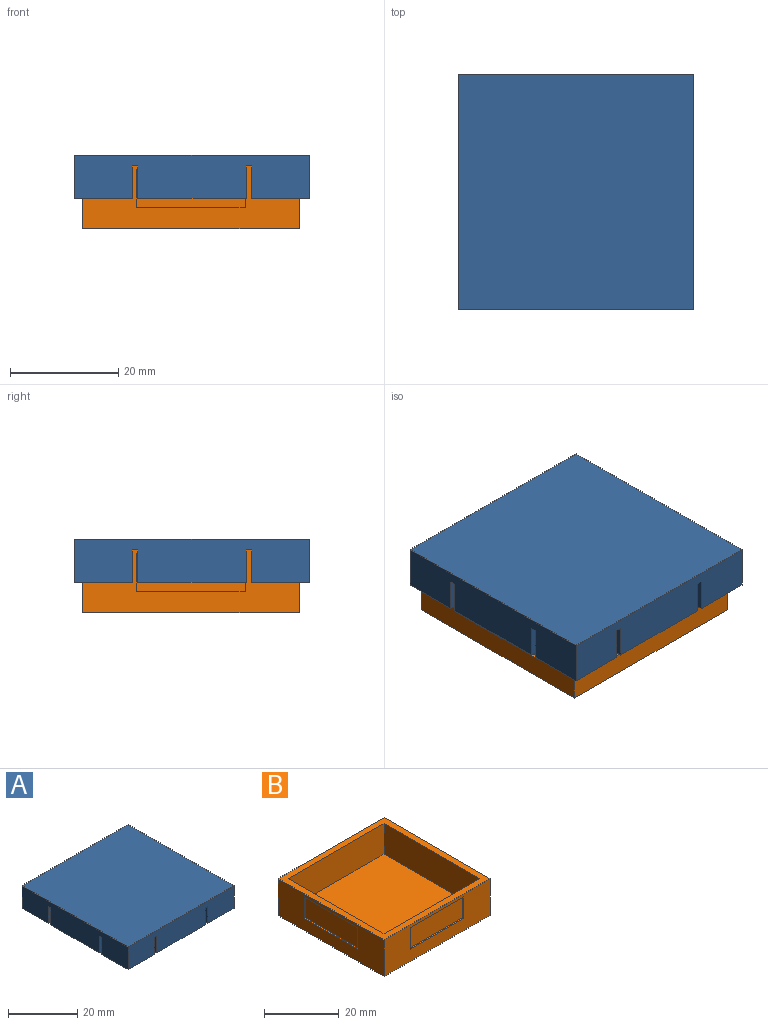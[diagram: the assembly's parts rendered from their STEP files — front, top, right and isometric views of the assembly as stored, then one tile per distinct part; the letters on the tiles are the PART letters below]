
ASSEMBLY  parts=2 mates=1
PART A: 66 faces, bbox 43.4x43.4x8 mm
  f0: plane 10.7x10.7mm, normal (0,0,-1), area 29.9mm2, adj f2,f3,f4,f7,f44,f58
  f1: plane 20x1.7mm, normal (0,0,-1), area 34mm2, adj f2,f54,f57,f64
  f2: plane 43.4x8mm, normal (-1,0,0), area 335.2mm2, adj f0,f1,f7,f12,f13,f16,f54,f55
  f3: plane 40.4x6.5mm, normal (1,0,0), area 190.6mm2, adj f0,f4,f12,f14,f17,f54,f55,f56
  f4: plane 40.4x6.5mm, normal (0,-1,0), area 190.6mm2, adj f0,f3,f5,f8,f17,f42,f43,f44
  f5: plane 10.7x10.7mm, normal (0,0,-1), area 29.9mm2, adj f4,f7,f8,f11,f32,f47
  f6: plane 20x1.7mm, normal (0,0,-1), area 34mm2, adj f7,f42,f46,f52
  f7: plane 43.4x8mm, normal (0,1,0), area 335.2mm2, adj f0,f2,f5,f6,f11,f16,f42,f43
  f8: plane 40.4x6.5mm, normal (-1,0,0), area 190.6mm2, adj f4,f5,f9,f14,f17,f30,f31,f32
  f9: plane 10.7x10.7mm, normal (0,0,-1), area 29.9mm2, adj f8,f11,f13,f14,f19,f35
  f10: plane 20x1.7mm, normal (0,0,-1), area 34mm2, adj f11,f30,f34,f40
  f11: plane 43.4x8mm, normal (1,0,0), area 335.2mm2, adj f5,f7,f9,f10,f13,f16,f30,f31
  f12: plane 10.7x10.7mm, normal (0,0,-1), area 29.9mm2, adj f2,f3,f13,f14,f22,f55
  f13: plane 43.4x8mm, normal (0,-1,0), area 335.2mm2, adj f2,f9,f11,f12,f15,f16,f18,f19
  f14: plane 40.4x6.5mm, normal (0,1,0), area 190.6mm2, adj f3,f8,f9,f12,f17,f18,f19,f20
  f15: plane 20x1.7mm, normal (0,0,-1), area 34mm2, adj f13,f18,f21,f28
  f16: plane 43.4x43.4mm, normal (0,0,1), area 1883.6mm2, adj f2,f7,f11,f13
  f17: plane 40.4x40.4mm, normal (0,0,-1), area 1632.2mm2, adj f3,f4,f8,f14
  f18: plane 6x1.7mm, normal (1,0,0), area 9.6mm2, adj f13,f14,f15,f20,f24,f26
  f19: plane 6x1.5mm, normal (-1,0,0), area 9mm2, adj f9,f13,f14,f20
  f20: plane 1.5x1mm, normal (0,0,-1), area 1.5mm2, adj f13,f14,f18,f19
  f21: plane 6x1.7mm, normal (-1,0,0), area 9.6mm2, adj f13,f14,f15,f23,f24,f29
  f22: plane 6x1.5mm, normal (1,0,0), area 9mm2, adj f12,f13,f14,f23
  f23: plane 1.5x1mm, normal (0,0,-1), area 1.5mm2, adj f13,f14,f21,f22
  f24: plane 20x0.2mm, normal (0,0,1), area 4mm2, adj f14,f18,f21,f27
  f25: plane 19.2x2.2mm, normal (0,1,0), area 42.2mm2, adj f26,f27,f28,f29
  f26: plane 3x0.4mm, normal (0.71,0.71,0), area 1.5mm2, adj f18,f25,f27,f28
  f27: plane 20x0.4mm, normal (0,0.71,0.71), area 11.1mm2, adj f24,f25,f26,f29
  f28: plane 20x0.4mm, normal (0,0.71,-0.71), area 11.1mm2, adj f15,f25,f26,f29
  f29: plane 3x0.4mm, normal (-0.71,0.71,0), area 1.5mm2, adj f21,f25,f27,f28
  f30: plane 6x1.7mm, normal (0,1,0), area 9.6mm2, adj f8,f10,f11,f31,f36,f41
  f31: plane 1.5x1mm, normal (0,0,-1), area 1.5mm2, adj f8,f11,f30,f32
  f32: plane 6x1.5mm, normal (0,-1,0), area 9mm2, adj f5,f8,f11,f31
  f33: plane 1.5x1mm, normal (0,0,-1), area 1.5mm2, adj f8,f11,f34,f35
  f34: plane 6x1.7mm, normal (0,-1,0), area 9.6mm2, adj f8,f10,f11,f33,f36,f38
  f35: plane 6x1.5mm, normal (0,1,0), area 9mm2, adj f8,f9,f11,f33
  f36: plane 20x0.2mm, normal (0,0,1), area 4mm2, adj f8,f30,f34,f39
  f37: plane 19.2x2.2mm, normal (-1,0,0), area 42.2mm2, adj f38,f39,f40,f41
  f38: plane 3x0.4mm, normal (-0.71,-0.71,0), area 1.5mm2, adj f34,f37,f39,f40
  f39: plane 20x0.4mm, normal (-0.71,0,0.71), area 11.1mm2, adj f36,f37,f38,f41
  f40: plane 20x0.4mm, normal (-0.71,0,-0.71), area 11.1mm2, adj f10,f37,f38,f41
  f41: plane 3x0.4mm, normal (-0.71,0.71,0), area 1.5mm2, adj f30,f37,f39,f40
  f42: plane 6x1.7mm, normal (-1,0,0), area 9.6mm2, adj f4,f6,f7,f43,f48,f53
  f43: plane 1.5x1mm, normal (0,0,-1), area 1.5mm2, adj f4,f7,f42,f44
  f44: plane 6x1.5mm, normal (1,0,0), area 9mm2, adj f0,f4,f7,f43
  f45: plane 1.5x1mm, normal (0,0,-1), area 1.5mm2, adj f4,f7,f46,f47
  f46: plane 6x1.7mm, normal (1,0,0), area 9.6mm2, adj f4,f6,f7,f45,f48,f50
  f47: plane 6x1.5mm, normal (-1,0,0), area 9mm2, adj f4,f5,f7,f45
  f48: plane 20x0.2mm, normal (0,0,1), area 4mm2, adj f4,f42,f46,f51
  f49: plane 19.2x2.2mm, normal (0,-1,0), area 42.2mm2, adj f50,f51,f52,f53
  f50: plane 3x0.4mm, normal (0.71,-0.71,0), area 1.5mm2, adj f46,f49,f51,f52
  f51: plane 20x0.4mm, normal (0,-0.71,0.71), area 11.1mm2, adj f48,f49,f50,f53
  f52: plane 20x0.4mm, normal (0,-0.71,-0.71), area 11.1mm2, adj f6,f49,f50,f53
  f53: plane 3x0.4mm, normal (-0.71,-0.71,0), area 1.5mm2, adj f42,f49,f51,f52
  f54: plane 6x1.7mm, normal (0,-1,0), area 9.6mm2, adj f1,f2,f3,f56,f60,f65
  f55: plane 6x1.5mm, normal (0,1,0), area 9mm2, adj f2,f3,f12,f56
  f56: plane 1.5x1mm, normal (0,0,-1), area 1.5mm2, adj f2,f3,f54,f55
  f57: plane 6x1.7mm, normal (0,1,0), area 9.6mm2, adj f1,f2,f3,f59,f60,f62
  f58: plane 6x1.5mm, normal (0,-1,0), area 9mm2, adj f0,f2,f3,f59
  f59: plane 1.5x1mm, normal (0,0,-1), area 1.5mm2, adj f2,f3,f57,f58
  f60: plane 20x0.2mm, normal (0,0,1), area 4mm2, adj f3,f54,f57,f63
  f61: plane 19.2x2.2mm, normal (1,0,0), area 42.2mm2, adj f62,f63,f64,f65
  f62: plane 3x0.4mm, normal (0.71,0.71,0), area 1.5mm2, adj f57,f61,f63,f64
  f63: plane 20x0.4mm, normal (0.71,0,0.71), area 11.1mm2, adj f60,f61,f62,f65
  f64: plane 20x0.4mm, normal (0.71,0,-0.71), area 11.1mm2, adj f1,f61,f62,f65
  f65: plane 3x0.4mm, normal (0.71,-0.71,0), area 1.5mm2, adj f54,f61,f63,f64
PART B: 31 faces, bbox 40x40x12 mm
  f0: plane 40x12mm, normal (0,1,0), area 340mm2, adj f1,f3,f4,f5,f26,f27,f28,f29
  f1: plane 40x12mm, normal (1,0,0), area 340mm2, adj f0,f2,f4,f5,f21,f22,f23,f24
  f2: plane 40x12mm, normal (0,-1,0), area 340mm2, adj f1,f3,f4,f5,f16,f17,f18,f19
  f3: plane 40x12mm, normal (-1,0,0), area 340mm2, adj f0,f2,f4,f5,f11,f12,f13,f14
  f4: plane 40x40mm, normal (0,0,1), area 304mm2, adj f0,f1,f2,f3,f6,f7,f8,f9
  f5: plane 40x40mm, normal (0,0,-1), area 1600mm2, adj f0,f1,f2,f3
  f6: plane 36x10mm, normal (1,0,0), area 360mm2, adj f4,f7,f9,f10
  f7: plane 36x10mm, normal (0,1,0), area 360mm2, adj f4,f6,f8,f10
  f8: plane 36x10mm, normal (-1,0,0), area 360mm2, adj f4,f7,f9,f10
  f9: plane 36x10mm, normal (0,-1,0), area 360mm2, adj f4,f6,f8,f10
  f10: plane 36x36mm, normal (0,0,1), area 1296mm2, adj f6,f7,f8,f9
  f11: plane 7x0.5mm, normal (0,-1,0), area 3.5mm2, adj f3,f12,f14,f15
  f12: plane 20x0.5mm, normal (0,0,1), area 10mm2, adj f3,f11,f13,f15
  f13: plane 7x0.5mm, normal (0,1,0), area 3.5mm2, adj f3,f12,f14,f15
  f14: plane 20x0.5mm, normal (0,0,-1), area 10mm2, adj f3,f11,f13,f15
  f15: plane 20x7mm, normal (-1,0,0), area 140mm2, adj f11,f12,f13,f14
  f16: plane 7x0.5mm, normal (1,0,0), area 3.5mm2, adj f2,f17,f19,f20
  f17: plane 20x0.5mm, normal (0,0,1), area 10mm2, adj f2,f16,f18,f20
  f18: plane 7x0.5mm, normal (-1,0,0), area 3.5mm2, adj f2,f17,f19,f20
  f19: plane 20x0.5mm, normal (0,0,-1), area 10mm2, adj f2,f16,f18,f20
  f20: plane 20x7mm, normal (0,-1,0), area 140mm2, adj f16,f17,f18,f19
  f21: plane 7x0.5mm, normal (0,1,0), area 3.5mm2, adj f1,f22,f24,f25
  f22: plane 20x0.5mm, normal (0,0,1), area 10mm2, adj f1,f21,f23,f25
  f23: plane 7x0.5mm, normal (0,-1,0), area 3.5mm2, adj f1,f22,f24,f25
  f24: plane 20x0.5mm, normal (0,0,-1), area 10mm2, adj f1,f21,f23,f25
  f25: plane 20x7mm, normal (1,0,0), area 140mm2, adj f21,f22,f23,f24
  f26: plane 7x0.5mm, normal (-1,0,0), area 3.5mm2, adj f0,f27,f29,f30
  f27: plane 20x0.5mm, normal (0,0,1), area 10mm2, adj f0,f26,f28,f30
  f28: plane 7x0.5mm, normal (1,0,0), area 3.5mm2, adj f0,f27,f29,f30
  f29: plane 20x0.5mm, normal (0,0,-1), area 10mm2, adj f0,f26,f28,f30
  f30: plane 20x7mm, normal (0,1,0), area 140mm2, adj f26,f27,f28,f29
PLACE A t=(0.2,-0.2,-6.38)mm
PLACE B at identity
MATE slider B.f4 <-> A.f17  axis (0,0,1) through (0,40,12)mm
